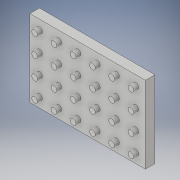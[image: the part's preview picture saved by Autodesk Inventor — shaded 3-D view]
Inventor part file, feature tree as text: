
AUTODESK INVENTOR PART (.ipt)
format: ipt  version: 2017 (Build 210142000, 142)  size: 142,336 bytes
history: native  units: in
note: dims shown in document units (in); Inventor stores cm internally (conversion verified against a paired STEP export)
features: extrude x2, sketch x2, pattern_linear x1
ambient origin geometry x8: Origin, YZ Plane, XZ Plane, XY Plane, X Axis, Y Axis, Z Axis, Center Point
bodies: Solid1 (feature_tree)
feature tree (5):
  extrude  "Extrusion1"  Depth=6.0in
  extrude  "Extrusion2"  Depth=0.25in
  pattern_linear  "Rectangular Pattern1"  Spacing1=0.25in  [1 undecoded]
  sketch  "Sketch1"  dims[d0=4.0in d1=6.0in]
  sketch  "Sketch2"  dims[d2=0.5in d3=0.0in d6=0.3in d7=0.25in d8=0.0in d9=1.5748in d11=1.0in d12=2.3622in d14=1.0in]
note: 1 required parameter value undecoded (feature->parameter linkage not recoverable at this tier; creation-order binding heuristic only, values carry confidence <= 0.55)
